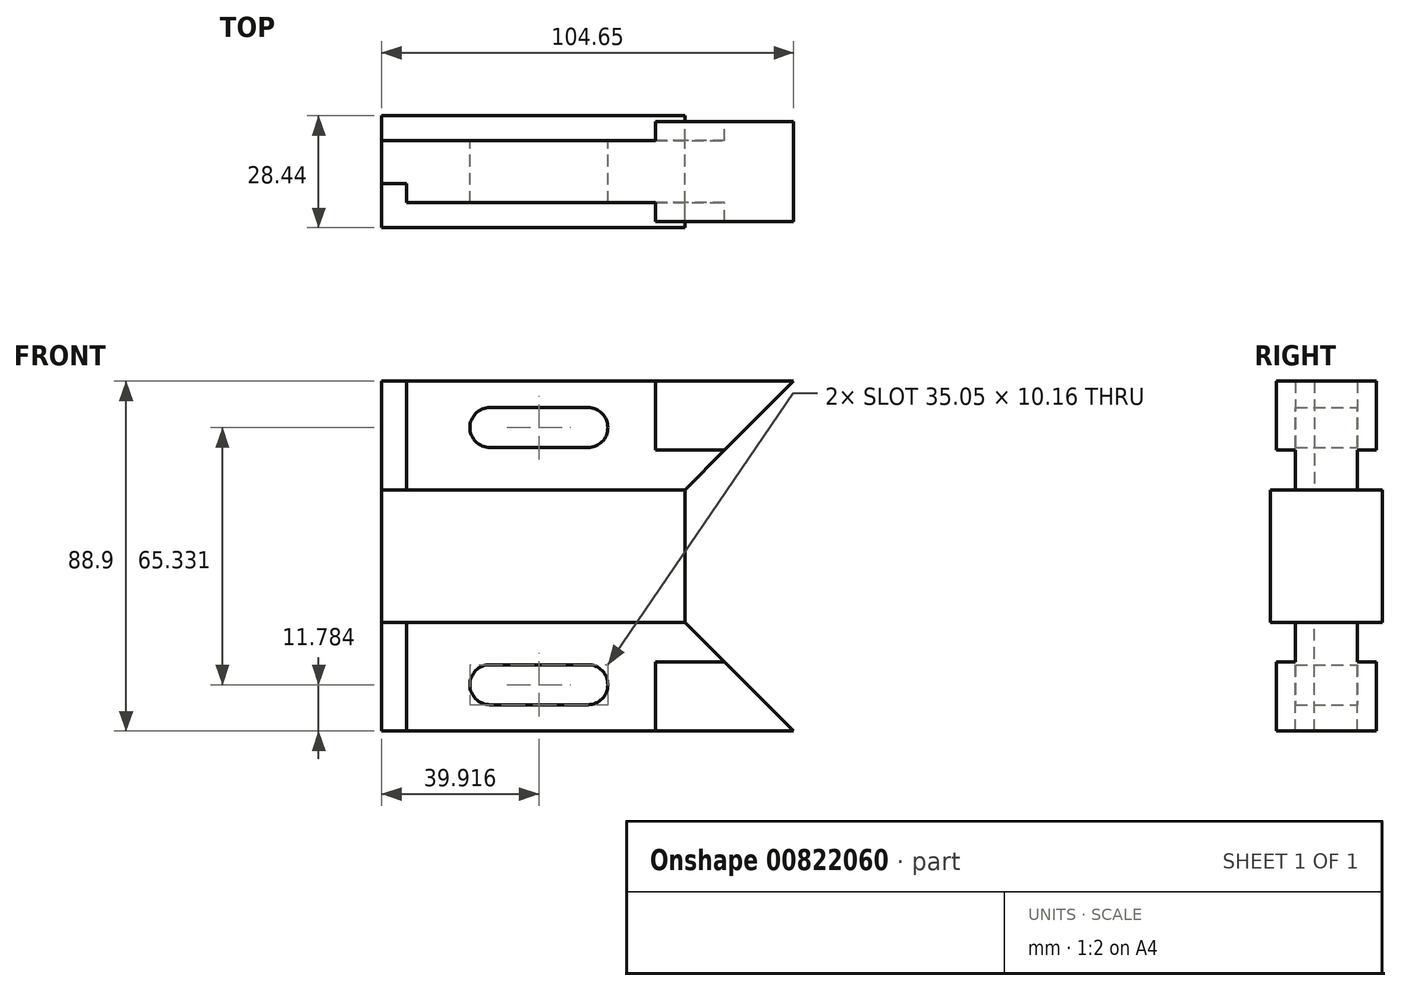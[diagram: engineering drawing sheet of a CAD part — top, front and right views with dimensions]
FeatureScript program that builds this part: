
annotation { "Feature Type Name" : "Feature", "Feature Type Description" : "" }
export const myFeature = defineFeature(function(context is Context, id is Id, definition is map)
    precondition{}
    {
        {
            var Q0;
            Q0=qCreatedBy(makeId("Front.planeOp"),FACE);
            var sketch = newSketch(context, id + "F0", { "sketchPlane" : qUnion([Q0])});
            skLineSegment(sketch, "E0", {"start": v(0, 44.45) * mm, "end": v(104.65, 44.45) * mm});
            skLineSegment(sketch, "E1", {"start": v(77.06, 16.86) * mm, "end": v(77.06, 0) * mm});
            skLineSegment(sketch, "E2", {"start": v(77.06, 16.86) * mm, "end": v(0, 16.86) * mm});
            skLineSegment(sketch, "E3", {"start": v(0, 0) * mm, "end": v(77.06, 0) * mm});
            skLineSegment(sketch, "E4", {"start": v(0, 44.45) * mm, "end": v(0, 0) * mm});
            skLineSegment(sketch, "E5", {"start": v(104.65, 44.45) * mm, "end": v(77.06, 16.86) * mm});
            skLineSegment(sketch, "E6", {"start": v(69.6, 44.45) * mm, "end": v(69.6, 26.92) * mm});
            skLineSegment(sketch, "E7", {"start": v(69.6, 26.92) * mm, "end": v(87.12, 26.92) * mm});
            skCircle(sketch, "E8", {"center": v(52.36, 32.67) * mm, "radius": 5.08 * mm});
            skCircle(sketch, "E9", {"center": v(27.47, 32.67) * mm, "radius": 5.08 * mm});
            skLineSegment(sketch, "E10", {"start": v(27.47, 27.59) * mm, "end": v(52.36, 27.59) * mm});
            skLineSegment(sketch, "E11", {"start": v(27.47, 37.75) * mm, "end": v(52.36, 37.75) * mm});
            skLineSegment(sketch, "E12", {"start": v(6.35, 44.45) * mm, "end": v(6.35, 16.86) * mm});
            skSolve(sketch);
        }
        {
            var Q0;
            {var subQ5=sQuery(id+"F0.wireOp",EDGE,"E1");Q0=makeQuery(id+"F0.imprint","IMPRINT",FACE,{"disambiguationData":[TD([[makeQuery(id+"F0.imprint","IMPRINT",EDGE,{"derivedFrom":subQ5}),-1.0]])]});}
            extrude(context, id + "F1", {"entities" : qUnion([Q0]), "endBound" : BoundingType.SYMMETRIC, "depth" : 28.45 * mm, "offsetDistance" : 25.4 * mm});
        }
        {
            var Q0;
            {var subQ3=sQuery(id+"F0.wireOp",EDGE,"E6");Q0=makeQuery(id+"F0.imprint","IMPRINT",FACE,{"disambiguationData":[TD([[makeQuery(id+"F0.imprint","IMPRINT",EDGE,{"derivedFrom":subQ3}),1.0]])]});}
            extrude(context, id + "F2", {"entities" : qUnion([Q0]), "operationType" : NewBodyOperationType.ADD, "endBound" : BoundingType.SYMMETRIC, "depth" : 25.4 * mm, "offsetDistance" : 25.4 * mm});
        }
        {
            var Q0;
            {var subQ8=sQuery(id+"F0.wireOp",EDGE,"E6");Q0=makeQuery(id+"F0.imprint","IMPRINT",FACE,{"disambiguationData":[TD([[makeQuery(id+"F0.imprint","IMPRINT",EDGE,{"derivedFrom":subQ8}),-1.0]])]});}
            extrude(context, id + "F3", {"entities" : qUnion([Q0]), "endBound" : BoundingType.SYMMETRIC, "depth" : 15.75 * mm, "offsetDistance" : 25.4 * mm});
        }
        {
            var Q0;
            {var subQ3=sQuery(id+"F0.wireOp",EDGE,"E12");Q0=makeQuery(id+"F0.imprint","IMPRINT",FACE,{"disambiguationData":[TD([[makeQuery(id+"F0.imprint","IMPRINT",EDGE,{"derivedFrom":subQ3}),-1.0]])]});}
            extrude(context, id + "F4", {"entities" : qUnion([Q0]), "endBound" : BoundingType.SYMMETRIC, "depth" : 15.75 * mm, "offsetDistance" : 25.4 * mm});
        }
        {
            var Q0;
            Q0=makeQuery(id+"F4.opExtrude","CAP_FACE",FACE,{"disambiguationData":[OSD([sQuery(id+"F0.wireOp",EDGE,"E0"),sQuery(id+"F0.wireOp",EDGE,"E2"),sQuery(id+"F0.wireOp",EDGE,"E4"),sQuery(id+"F0.wireOp",EDGE,"E12")])],"isStart":false});
            extrude(context, id + "F5", {"entities" : qUnion([Q0]), "operationType" : NewBodyOperationType.REMOVE, "oppositeDirection" : true, "depth" : 4.83 * mm, "offsetDistance" : 25.4 * mm});
        }
        {
            var Q0;
            Q0=makeQuery(id+"F1.opExtrude","SWEPT_BODY",BODY,{"disambiguationData":[OSD([sQuery(id+"F0.wireOp",EDGE,"E1"),sQuery(id+"F0.wireOp",EDGE,"E2"),sQuery(id+"F0.wireOp",EDGE,"E3"),sQuery(id+"F0.wireOp",EDGE,"E4")])]});
            var Q1;
            Q1=makeQuery(id+"F2.opExtrude","SWEPT_BODY",BODY,{"disambiguationData":[OSD([sQuery(id+"F0.wireOp",EDGE,"E0"),sQuery(id+"F0.wireOp",EDGE,"E5"),sQuery(id+"F0.wireOp",EDGE,"E6"),sQuery(id+"F0.wireOp",EDGE,"E7")])]});
            var Q2;
            Q2=makeQuery(id+"F3.opExtrude","SWEPT_BODY",BODY,{"disambiguationData":[OSD([sQuery(id+"F0.wireOp",EDGE,"E0"),sQuery(id+"F0.wireOp",EDGE,"E2"),sQuery(id+"F0.wireOp",EDGE,"E5"),sQuery(id+"F0.wireOp",EDGE,"E6"),sQuery(id+"F0.wireOp",EDGE,"E7"),sQuery(id+"F0.wireOp",EDGE,"E8"),sQuery(id+"F0.wireOp",EDGE,"E9"),sQuery(id+"F0.wireOp",EDGE,"E10"),sQuery(id+"F0.wireOp",EDGE,"E11"),sQuery(id+"F0.wireOp",EDGE,"E12")])]});
            var Q3;
            Q3=makeQuery(id+"F4.opExtrude","SWEPT_BODY",BODY,{"disambiguationData":[OSD([sQuery(id+"F0.wireOp",EDGE,"E0"),sQuery(id+"F0.wireOp",EDGE,"E2"),sQuery(id+"F0.wireOp",EDGE,"E4"),sQuery(id+"F0.wireOp",EDGE,"E12")])]});
            var Q4;
            Q4=makeQuery(id+"F1.opExtrude","SWEPT_FACE",FACE,{"disambiguationData":[OSD([sQuery(id+"F0.wireOp",EDGE,"E3")])]});
            mirror(context, id + "F6", {"operationType" : NewBodyOperationType.ADD, "entities" : qUnion([Q0, Q1, Q2, Q3]), "mirrorPlane" : qUnion([Q4])});
        }
    });
